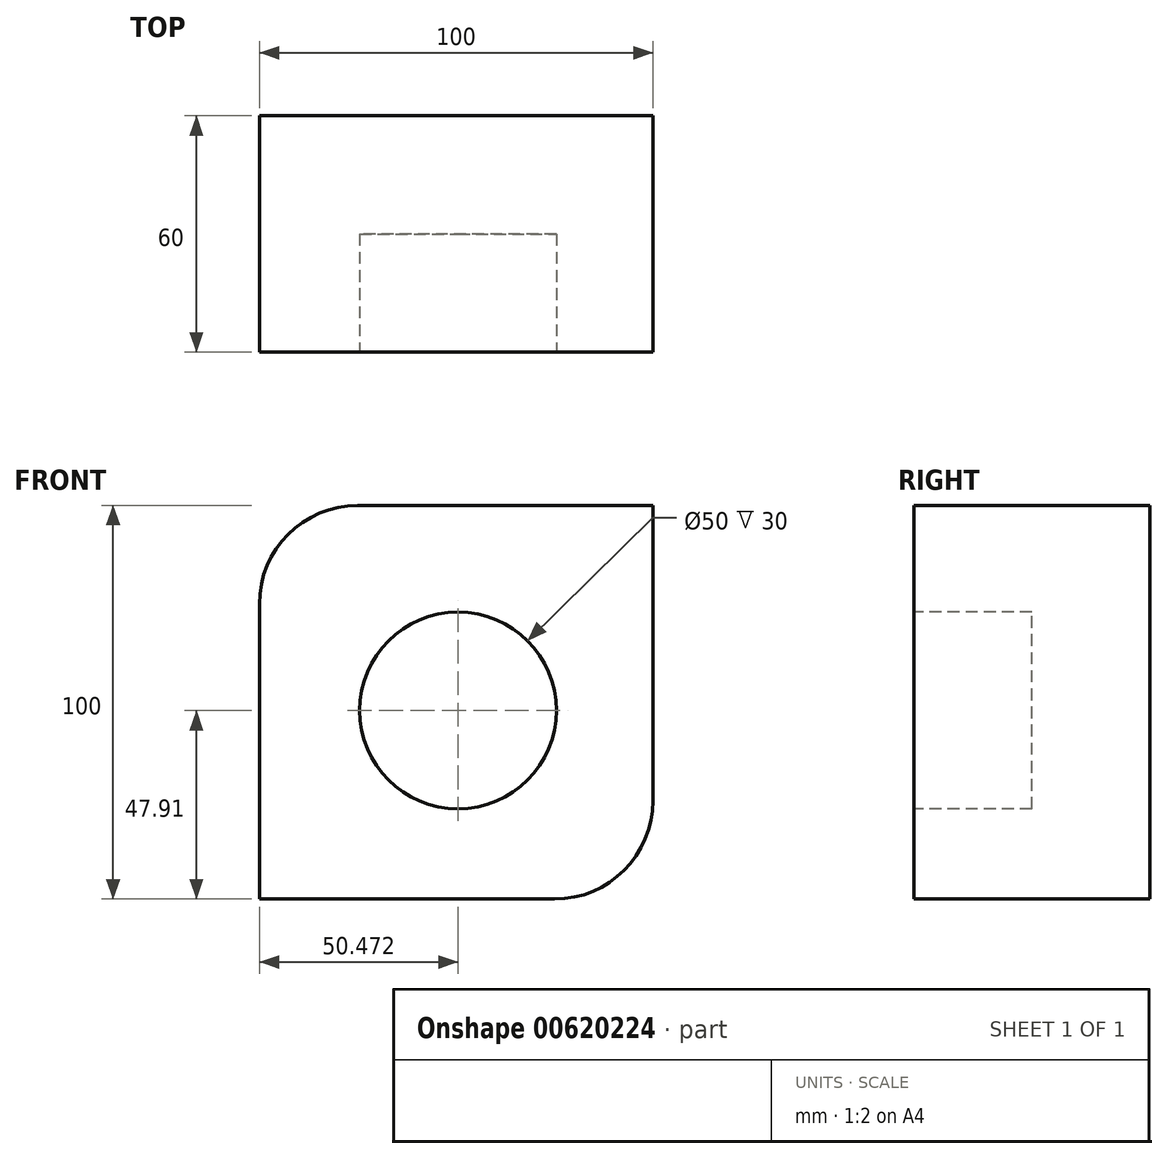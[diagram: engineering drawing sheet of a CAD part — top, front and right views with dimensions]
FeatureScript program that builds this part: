
annotation { "Feature Type Name" : "Feature", "Feature Type Description" : "" }
export const myFeature = defineFeature(function(context is Context, id is Id, definition is map)
    precondition{}
    {
        {
            var Q0;
            Q0=qCreatedBy(makeId("Front.planeOp"),FACE);
            var sketch = newSketch(context, id + "F0", { "sketchPlane" : qUnion([Q0])});
            skLineSegment(sketch, "E0.bottom", {"start": v(-17.84, 52.09) * mm, "end": v(57.16, 52.09) * mm});
            skLineSegment(sketch, "E0.top", {"start": v(-42.84, -47.91) * mm, "end": v(32.16, -47.91) * mm});
            skLineSegment(sketch, "E0.left", {"start": v(-42.84, 27.09) * mm, "end": v(-42.84, -47.91) * mm});
            skLineSegment(sketch, "E0.right", {"start": v(57.16, 52.09) * mm, "end": v(57.16, -22.91) * mm});
            skPoint(sketch, "E1.visualSharp", {"position": v(-42.84, 52.09) * mm});
            skArc(sketch, "E1.filletArc", {"start": v(-17.84, 52.09) * mm, "mid": v(-35.52, 44.76) * mm, "end": v(-42.84, 27.09) * mm});
            skPoint(sketch, "E2.visualSharp", {"position": v(57.16, -47.91) * mm});
            skArc(sketch, "E2.filletArc", {"start": v(32.16, -47.91) * mm, "mid": v(49.84, -40.6) * mm, "end": v(57.16, -22.91) * mm});
            skSolve(sketch);
        }
        {
            var Q0;
            Q0=makeQuery(id+"F0.imprint","IMPRINT",FACE,{"disambiguationData":[TD([[makeQuery(id+"F0.imprint","IMPRINT",EDGE,{"derivedFrom":sQuery(id+"F0.wireOp",EDGE,"E0.bottom")}),-1.0]])]});
            extrude(context, id + "F1", {"entities" : qUnion([Q0]), "depth" : 60 * mm, "offsetDistance" : 25 * mm});
        }
        {
            var Q0;
            Q0=makeQuery(id+"F1.opExtrude","CAP_FACE",FACE,{"disambiguationData":[OSD([sQuery(id+"F0.wireOp",EDGE,"E0.bottom"),sQuery(id+"F0.wireOp",EDGE,"E0.top"),sQuery(id+"F0.wireOp",EDGE,"E0.left"),sQuery(id+"F0.wireOp",EDGE,"E0.right"),sQuery(id+"F0.wireOp",EDGE,"E1.filletArc"),sQuery(id+"F0.wireOp",EDGE,"E2.filletArc")])],"isStart":false});
            var sketch = newSketch(context, id + "F2", { "sketchPlane" : qUnion([Q0])});
            skCircle(sketch, "E3", {"center": v(7.63, 0) * mm, "radius": 25 * mm});
            skSolve(sketch);
        }
        {
            var Q0;
            Q0=makeQuery(id+"F2.imprint","IMPRINT",FACE,{"disambiguationData":[TD([[makeQuery(id+"F2.imprint","IMPRINT",EDGE,{"derivedFrom":sQuery(id+"F2.wireOp",EDGE,"E3")}),1.0]])]});
            extrude(context, id + "F3", {"entities" : qUnion([Q0]), "operationType" : NewBodyOperationType.REMOVE, "oppositeDirection" : true, "depth" : 30 * mm, "offsetDistance" : 25 * mm});
        }
    });
